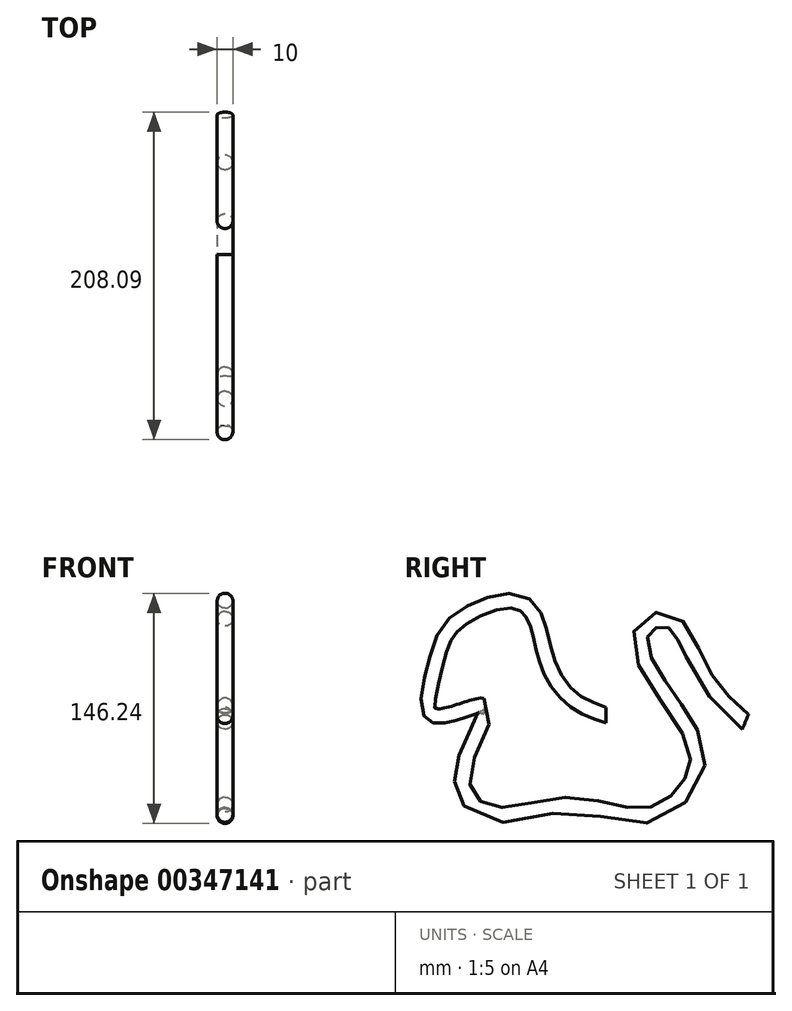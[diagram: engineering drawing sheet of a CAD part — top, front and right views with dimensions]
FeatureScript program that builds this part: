
annotation { "Feature Type Name" : "Feature", "Feature Type Description" : "" }
export const myFeature = defineFeature(function(context is Context, id is Id, definition is map)
    precondition{}
    {
        {
            var Q0;
            Q0=qCreatedBy(makeId("Front.planeOp"),FACE);
            var sketch = newSketch(context, id + "F0", { "sketchPlane" : qUnion([Q0])});
            skCircle(sketch, "E0", {"center": v(0, 0) * mm, "radius": 5 * mm});
            skSolve(sketch);
        }
        {
            var Q0;
            Q0=qCreatedBy(makeId("Right.planeOp"),FACE);
            var sketch = newSketch(context, id + "F1", { "sketchPlane" : qUnion([Q0])});
            skFitSpline(sketch, "E1", {"points": [v(0, 0) * mm, v(-21.6, 10.44) * mm, v(-36.55, 31.9) * mm, v(-42.76, 55.32) * mm, v(-56.6, 72.26) * mm, v(-96.1, 58.15) * mm, v(-108.25, 32.18) * mm, v(-109.1, 0) * mm, v(-77.2, 5.65) * mm, v(-91.31, -36.98) * mm, v(-72.68, -62.66) * mm, v(-23, -56.73) * mm, v(24.42, -63.8) * mm, v(52.36, -45.44) * mm, v(55.18, -14.4) * mm, v(21.31, 48.27) * mm, v(39.37, 60.69) * mm, v(61.1, 26.81) * mm, v(88.49, -4.23) * mm], "startDerivative": vector(-496.43, 173.37) * mm, "endDerivative": vector(496.07, -438.22) * mm});
            skSolve(sketch);
        }
        {
            var Q0;
            Q0=makeQuery(id+"F0.imprint","IMPRINT",FACE,{"disambiguationData":[TD([[makeQuery(id+"F0.imprint","IMPRINT",EDGE,{"derivedFrom":sQuery(id+"F0.wireOp",EDGE,"E0")}),1.0]])]});
            var Q1;
            Q1=sQuery(id+"F1.wireOp",EDGE,"E1");
            sweep(context, id + "F2", {"profiles" : qUnion([Q0]), "path" : qUnion([Q1])});
        }
        {
            var Q0;
            Q0=makeQuery(id+"F2.opSweep","CAP_FACE",FACE,{"disambiguationData":[OSD([sQuery(id+"F0.wireOp",EDGE,"E0"),sQuery(id+"F1.wireOp",VERTEX,"E1.end")])],"isStart":false});
            var sketch = newSketch(context, id + "F3", { "sketchPlane" : qUnion([Q0])});
            skCircle(sketch, "E2.0", {"center": v(0, 29.52) * mm, "radius": 10 * mm});
            skSolve(sketch);
        }
        {
            var Q0;
            Q0=makeQuery(id+"F3.imprint","IMPRINT",FACE,{"disambiguationData":[TD([[makeQuery(id+"F3.imprint","IMPRINT",EDGE,{"derivedFrom":sQuery(id+"F3.wireOp",EDGE,"E2.0")}),1.0]])]});
            extrude(context, id + "F4", {"entities" : qUnion([Q0]), "depth" : 25 * mm, "hasDraft" : true, "draftAngle" : 10 * degree, "draftPullDirection" : true});
        }
        {
            var Q0;
            Q0=makeQuery(id+"F4.opExtrude","SWEPT_BODY",BODY,{"disambiguationData":[OSD([sQuery(id+"F0.wireOp",EDGE,"E0"),sQuery(id+"F1.wireOp",VERTEX,"E1.end"),sQuery(id+"F3.wireOp",EDGE,"E2.0")])]});
            deleteBodies(context, id + "F5", {"entities" : qUnion([Q0])});
        }
    });
